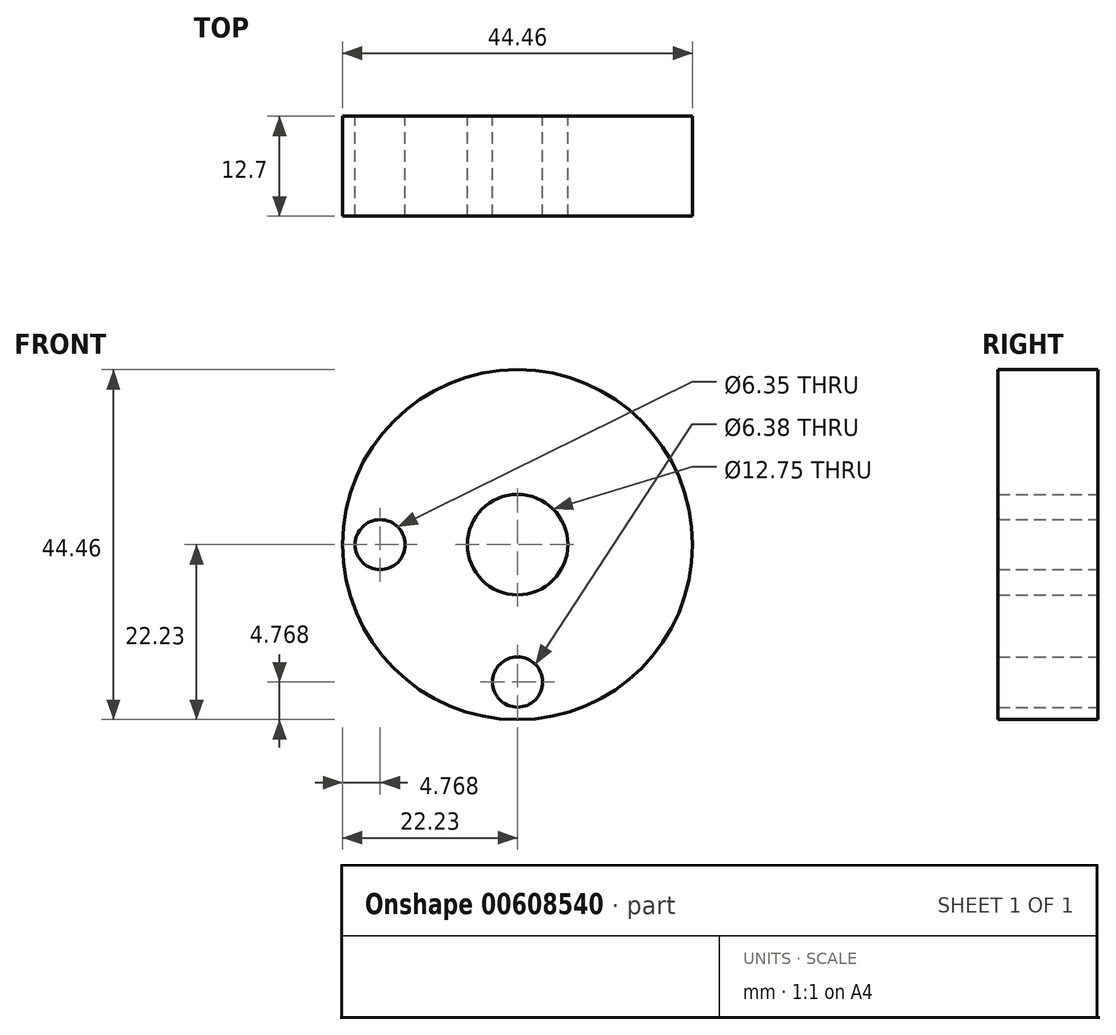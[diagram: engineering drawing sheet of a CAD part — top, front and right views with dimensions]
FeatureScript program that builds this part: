
annotation { "Feature Type Name" : "Feature", "Feature Type Description" : "" }
export const myFeature = defineFeature(function(context is Context, id is Id, definition is map)
    precondition{}
    {
        {
            var Q0;
            Q0=qCreatedBy(makeId("Front.planeOp"),FACE);
            var sketch = newSketch(context, id + "F0", { "sketchPlane" : qUnion([Q0])});
            skCircle(sketch, "E0", {"center": v(0, 0) * mm, "radius": 22.23 * mm});
            skCircle(sketch, "E1", {"center": v(-17.46, 0) * mm, "radius": 3.18 * mm});
            skCircle(sketch, "E2", {"center": v(0, -17.46) * mm, "radius": 3.19 * mm});
            skCircle(sketch, "E3", {"center": v(0, 0) * mm, "radius": 6.38 * mm});
            skSolve(sketch);
        }
        {
            var Q0;
            Q0=makeQuery(id+"F0.imprint","IMPRINT",FACE,{"disambiguationData":[TD([[makeQuery(id+"F0.imprint","IMPRINT",EDGE,{"derivedFrom":sQuery(id+"F0.wireOp",EDGE,"E0")}),1.0]])]});
            extrude(context, id + "F1", {"entities" : qUnion([Q0]), "depth" : 12.7 * mm, "offsetDistance" : 25.4 * mm});
        }
    });
